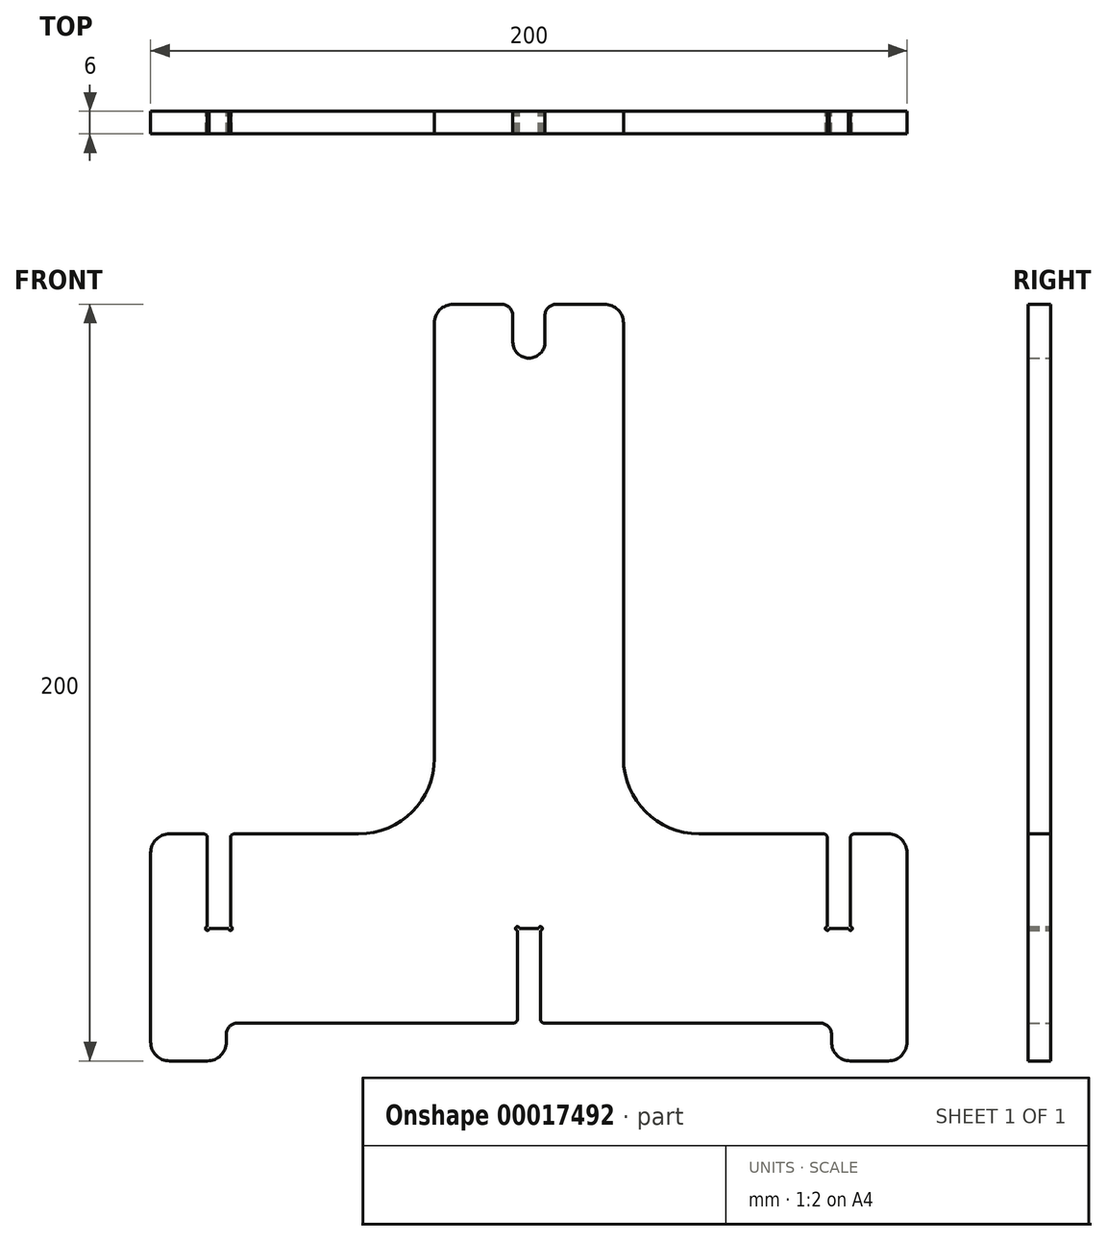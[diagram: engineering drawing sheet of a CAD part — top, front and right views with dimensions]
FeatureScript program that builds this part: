
annotation { "Feature Type Name" : "Feature", "Feature Type Description" : "" }
export const myFeature = defineFeature(function(context is Context, id is Id, definition is map)
    precondition{}
    {
        {
            var Q0;
            Q0=qCreatedBy(makeId("Front.planeOp"),FACE);
            var sketch = newSketch(context, id + "F0", { "sketchPlane" : qUnion([Q0])});
            skLineSegment(sketch, "E0.bottom", {"start": v(-95, 0) * mm, "end": v(-85, 0) * mm});
            skLineSegment(sketch, "E0.top", {"start": v(-95, 60) * mm, "end": v(-86, 60) * mm});
            skLineSegment(sketch, "E0.left", {"start": v(-100, 5) * mm, "end": v(-100, 55) * mm});
            skLineSegment(sketch, "E0.right", {"start": v(100, 5) * mm, "end": v(100, 55) * mm});
            skLineSegment(sketch, "E1", {"start": v(0, 0) * mm, "end": v(0, 214.81) * mm, "construction": true});
            skLineSegment(sketch, "E2.top", {"start": v(-20, 200) * mm, "end": v(-7.25, 200) * mm});
            skLineSegment(sketch, "E2.left", {"start": v(-25, 80) * mm, "end": v(-25, 195) * mm});
            skLineSegment(sketch, "E2.right", {"start": v(25, 80) * mm, "end": v(25, 195) * mm});
            skLineSegment(sketch, "E3.top", {"start": v(-77, 10) * mm, "end": v(-4.05, 10) * mm});
            skLineSegment(sketch, "E3.left", {"start": v(-80, 5) * mm, "end": v(-80, 7) * mm});
            skLineSegment(sketch, "E3.right", {"start": v(80, 5) * mm, "end": v(80, 7) * mm});
            skLineSegment(sketch, "E4.trimOffspring", {"start": v(85, 0) * mm, "end": v(95, 0) * mm});
            skLineSegment(sketch, "E5.left", {"start": v(-4.25, 197) * mm, "end": v(-4.25, 190) * mm});
            skLineSegment(sketch, "E5.right", {"start": v(4.25, 197) * mm, "end": v(4.25, 190) * mm});
            skArc(sketch, "E6", {"start": v(-4.25, 190) * mm, "mid": v(0, 185.75) * mm, "end": v(4.25, 190) * mm});
            skLineSegment(sketch, "E7.trimOffspring", {"start": v(7.25, 200) * mm, "end": v(20, 200) * mm});
            skPoint(sketch, "E8.visualSharp", {"position": v(-25, 200) * mm});
            skArc(sketch, "E8.filletArc", {"start": v(-20, 200) * mm, "mid": v(-23.54, 198.54) * mm, "end": v(-25, 195) * mm});
            skPoint(sketch, "E9.visualSharp", {"position": v(-25, 60) * mm});
            skArc(sketch, "E9.filletArc", {"start": v(-45, 60) * mm, "mid": v(-30.86, 65.86) * mm, "end": v(-25, 80) * mm});
            skPoint(sketch, "E10.visualSharp", {"position": v(-100, 60) * mm});
            skArc(sketch, "E10.filletArc", {"start": v(-95, 60) * mm, "mid": v(-98.54, 58.54) * mm, "end": v(-100, 55) * mm});
            skPoint(sketch, "E11.visualSharp", {"position": v(-100, 0) * mm});
            skArc(sketch, "E11.filletArc", {"start": v(-100, 5) * mm, "mid": v(-98.54, 1.46) * mm, "end": v(-95, 0) * mm});
            skPoint(sketch, "E12.visualSharp", {"position": v(-80, 0) * mm});
            skArc(sketch, "E12.filletArc", {"start": v(-85, 0) * mm, "mid": v(-81.46, 1.46) * mm, "end": v(-80, 5) * mm});
            skPoint(sketch, "E13.visualSharp", {"position": v(80, 0) * mm});
            skArc(sketch, "E13.filletArc", {"start": v(80, 5) * mm, "mid": v(81.46, 1.46) * mm, "end": v(85, 0) * mm});
            skPoint(sketch, "E14.visualSharp", {"position": v(100, 0) * mm});
            skArc(sketch, "E14.filletArc", {"start": v(95, 0) * mm, "mid": v(98.54, 1.46) * mm, "end": v(100, 5) * mm});
            skPoint(sketch, "E15.visualSharp", {"position": v(100, 60) * mm});
            skArc(sketch, "E15.filletArc", {"start": v(100, 55) * mm, "mid": v(98.54, 58.54) * mm, "end": v(95, 60) * mm});
            skPoint(sketch, "E16.visualSharp", {"position": v(25, 60) * mm});
            skArc(sketch, "E16.filletArc", {"start": v(25, 80) * mm, "mid": v(30.86, 65.86) * mm, "end": v(45, 60) * mm});
            skPoint(sketch, "E17.visualSharp", {"position": v(25, 200) * mm});
            skArc(sketch, "E17.filletArc", {"start": v(25, 195) * mm, "mid": v(23.54, 198.54) * mm, "end": v(20, 200) * mm});
            skPoint(sketch, "E18.visualSharp", {"position": v(4.25, 200) * mm});
            skArc(sketch, "E18.filletArc", {"start": v(7.25, 200) * mm, "mid": v(5.13, 199.12) * mm, "end": v(4.25, 197) * mm});
            skPoint(sketch, "E19.visualSharp", {"position": v(-4.25, 200) * mm});
            skArc(sketch, "E19.filletArc", {"start": v(-4.25, 197) * mm, "mid": v(-5.13, 199.12) * mm, "end": v(-7.25, 200) * mm});
            skPoint(sketch, "E20.visualSharp", {"position": v(-80, 10) * mm});
            skArc(sketch, "E20.filletArc", {"start": v(-77, 10) * mm, "mid": v(-79.12, 9.12) * mm, "end": v(-80, 7) * mm});
            skPoint(sketch, "E21.visualSharp", {"position": v(80, 10) * mm});
            skArc(sketch, "E21.filletArc", {"start": v(80, 7) * mm, "mid": v(79.12, 9.12) * mm, "end": v(77, 10) * mm});
            skLineSegment(sketch, "E22.top", {"start": v(-84.5, 35) * mm, "end": v(-79.4, 35) * mm});
            skLineSegment(sketch, "E22.left", {"start": v(-85, 59) * mm, "end": v(-85, 35.5) * mm});
            skLineSegment(sketch, "E22.right", {"start": v(-78.9, 59) * mm, "end": v(-78.9, 35.5) * mm});
            skLineSegment(sketch, "E23.top", {"start": v(79.4, 35) * mm, "end": v(84.5, 35) * mm});
            skLineSegment(sketch, "E23.left", {"start": v(78.9, 59) * mm, "end": v(78.9, 35.5) * mm});
            skLineSegment(sketch, "E23.right", {"start": v(85, 59) * mm, "end": v(85, 35.5) * mm});
            skLineSegment(sketch, "E24.trimOffspring", {"start": v(-77.9, 60) * mm, "end": v(-45, 60) * mm});
            skLineSegment(sketch, "E25.trimOffspring", {"start": v(86, 60) * mm, "end": v(95, 60) * mm});
            skLineSegment(sketch, "E26", {"start": v(45, 60) * mm, "end": v(77.9, 60) * mm});
            skPoint(sketch, "E27.visualSharp", {"position": v(-85, 60) * mm});
            skArc(sketch, "E27.filletArc", {"start": v(-85, 59) * mm, "mid": v(-85.3, 59.7) * mm, "end": v(-86, 60) * mm});
            skPoint(sketch, "E28.visualSharp", {"position": v(-78.9, 60) * mm});
            skArc(sketch, "E28.filletArc", {"start": v(-77.9, 60) * mm, "mid": v(-78.6, 59.7) * mm, "end": v(-78.9, 59) * mm});
            skPoint(sketch, "E29.visualSharp", {"position": v(78.9, 60) * mm});
            skArc(sketch, "E29.filletArc", {"start": v(78.9, 59) * mm, "mid": v(78.6, 59.7) * mm, "end": v(77.9, 60) * mm});
            skPoint(sketch, "E30.visualSharp", {"position": v(85, 60) * mm});
            skArc(sketch, "E30.filletArc", {"start": v(86, 60) * mm, "mid": v(85.3, 59.7) * mm, "end": v(85, 59) * mm});
            skArc(sketch, "E31", {"start": v(-85, 35.5) * mm, "mid": v(-85.35, 34.65) * mm, "end": v(-84.5, 35) * mm});
            skArc(sketch, "E32", {"start": v(-79.4, 35) * mm, "mid": v(-78.55, 34.65) * mm, "end": v(-78.9, 35.5) * mm});
            skArc(sketch, "E33", {"start": v(78.9, 35.5) * mm, "mid": v(78.55, 34.65) * mm, "end": v(79.4, 35) * mm});
            skArc(sketch, "E34", {"start": v(84.5, 35) * mm, "mid": v(85.35, 34.65) * mm, "end": v(85, 35.5) * mm});
            skLineSegment(sketch, "E35.top", {"start": v(-2.55, 35) * mm, "end": v(2.55, 35) * mm});
            skLineSegment(sketch, "E35.left", {"start": v(-3.05, 11) * mm, "end": v(-3.05, 34.5) * mm});
            skLineSegment(sketch, "E35.right", {"start": v(3.05, 11) * mm, "end": v(3.05, 34.5) * mm});
            skLineSegment(sketch, "E36.trimOffspring", {"start": v(4.05, 10) * mm, "end": v(77, 10) * mm});
            skArc(sketch, "E37", {"start": v(-2.55, 35) * mm, "mid": v(-3.4, 35.35) * mm, "end": v(-3.05, 34.5) * mm});
            skArc(sketch, "E38", {"start": v(3.05, 34.5) * mm, "mid": v(3.4, 35.35) * mm, "end": v(2.55, 35) * mm});
            skPoint(sketch, "E39.visualSharp", {"position": v(-3.05, 10) * mm});
            skArc(sketch, "E39.filletArc", {"start": v(-4.05, 10) * mm, "mid": v(-3.34, 10.3) * mm, "end": v(-3.05, 11) * mm});
            skPoint(sketch, "E40.visualSharp", {"position": v(3.05, 10) * mm});
            skArc(sketch, "E40.filletArc", {"start": v(3.05, 11) * mm, "mid": v(3.34, 10.3) * mm, "end": v(4.05, 10) * mm});
            skSolve(sketch);
        }
        {
            var Q0;
            Q0 = qSketchRegion(id + "F0", true);
            extrude(context, id + "F1", {"entities" : qUnion([Q0]), "depth" : 6 * mm});
        }
    });
